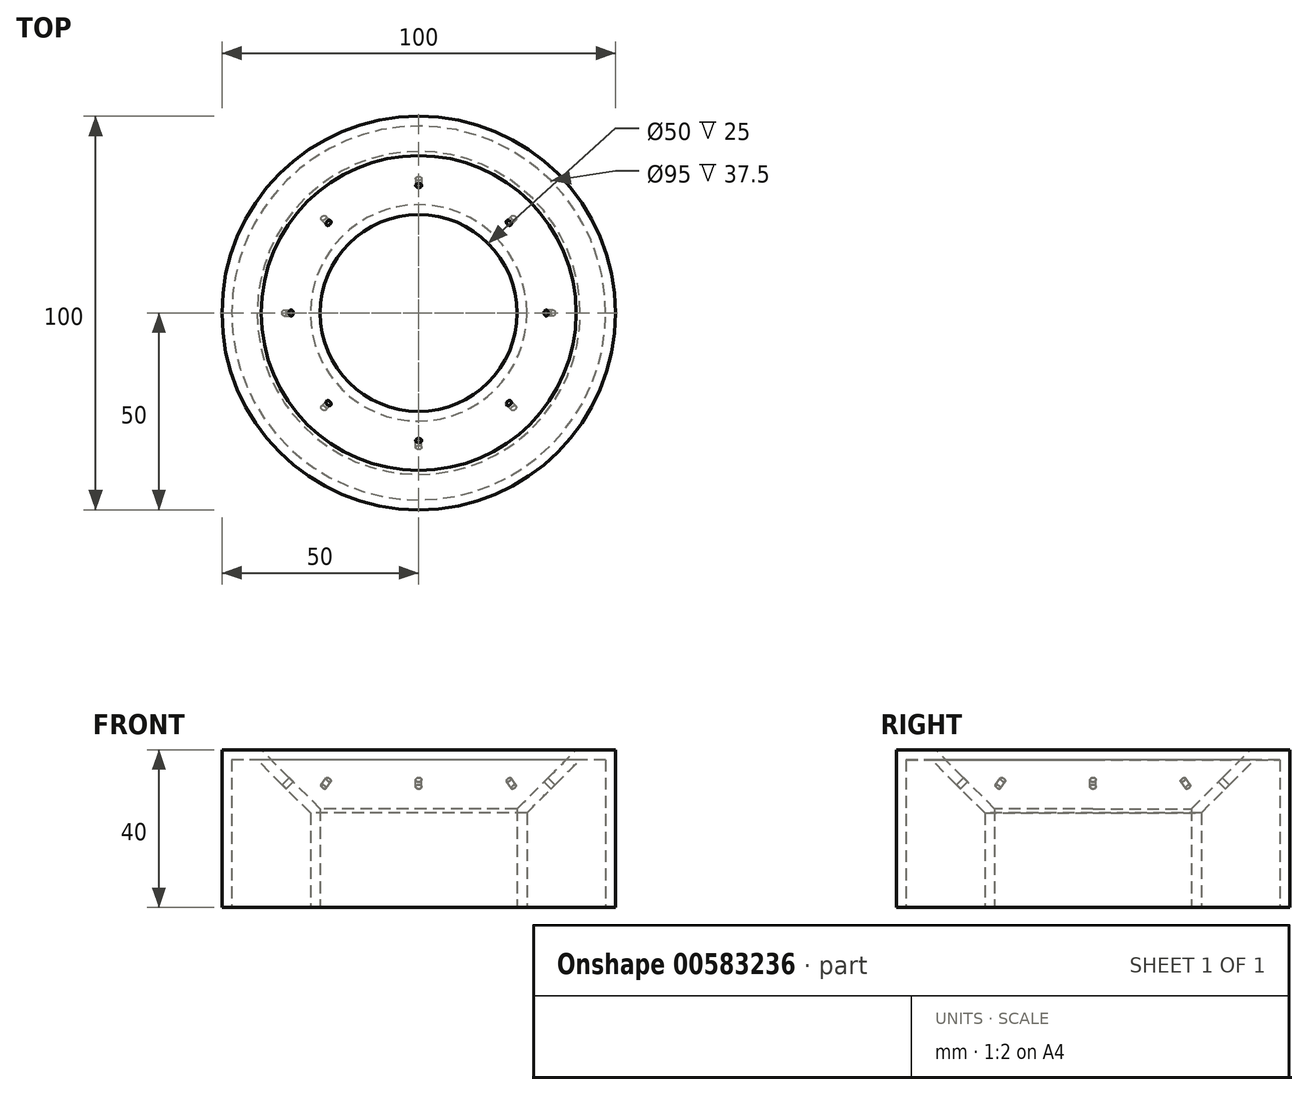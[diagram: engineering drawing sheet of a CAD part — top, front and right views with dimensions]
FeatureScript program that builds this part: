
annotation { "Feature Type Name" : "Feature", "Feature Type Description" : "" }
export const myFeature = defineFeature(function(context is Context, id is Id, definition is map)
    precondition{}
    {
        {
            var Q0;
            Q0=qCreatedBy(makeId("Top.planeOp"),FACE);
            var sketch = newSketch(context, id + "F0", { "sketchPlane" : qUnion([Q0])});
            skCircle(sketch, "E0", {"center": v(0, 0) * mm, "radius": 50 * mm});
            skSolve(sketch);
        }
        {
            var Q0;
            Q0=qSketchRegion(id+"F0",true);
            extrude(context, id + "F1", {"entities" : qUnion([Q0]), "depth" : 40 * mm, "offsetDistance" : 25 * mm});
        }
        {
            var Q0;
            Q0=makeQuery(id+"F1.opExtrude","CAP_FACE",FACE,{"disambiguationData":[OSD([sQuery(id+"F0.wireOp",EDGE,"E0")])],"isStart":true});
            var sketch = newSketch(context, id + "F2", { "sketchPlane" : qUnion([Q0])});
            skCircle(sketch, "E1.0", {"center": v(0, 0) * mm, "radius": 25 * mm});
            skSolve(sketch);
        }
        {
            var Q0;
            Q0=makeQuery(id+"F2.imprint","IMPRINT",FACE,{"disambiguationData":[TD([[makeQuery(id+"F2.imprint","IMPRINT",EDGE,{"derivedFrom":sQuery(id+"F2.wireOp",EDGE,"E1.0")}),1.0]])]});
            extrude(context, id + "F3", {"entities" : qUnion([Q0]), "operationType" : NewBodyOperationType.REMOVE, "oppositeDirection" : true, "depth" : 50 * mm, "offsetDistance" : 25 * mm});
        }
        {
            var Q0;
            Q0=makeQuery(id+"F1.opExtrude","CAP_FACE",FACE,{"disambiguationData":[OSD([sQuery(id+"F0.wireOp",EDGE,"E0")])],"isStart":false});
            var sketch = newSketch(context, id + "F4", { "sketchPlane" : qUnion([Q0])});
            skCircle(sketch, "E2.0", {"center": v(0, 0) * mm, "radius": 40 * mm});
            skSolve(sketch);
        }
        {
            var Q0;
            Q0=makeQuery(id+"F3.boolean.opBoolean","INTERSECT",EDGE,{"derivedFrom":[makeQuery(id+"F1.opExtrude","CAP_FACE",FACE,{"disambiguationData":[OSD([sQuery(id+"F0.wireOp",EDGE,"E0")])],"isStart":false}),makeQuery(id+"F3.opExtrude","SWEPT_FACE",FACE,{"disambiguationData":[OSD([sQuery(id+"F2.wireOp",EDGE,"E1.0")])]})]});
            chamfer(context, id + "F5", {"entities" : qUnion([Q0]), "width" : 15 * mm, "tangentPropagation" : true});
        }
        {
            var Q0;
            Q0=makeQuery(id+"F1.opExtrude","CAP_FACE",FACE,{"disambiguationData":[OSD([sQuery(id+"F0.wireOp",EDGE,"E0")])],"isStart":true});
            shell(context, id + "F6", {"entities" : qUnion([Q0]), "thickness" : 2.5 * mm});
        }
        {
            var Q0;
            Q0=makeQuery(id+"F4.imprint","IMPRINT",FACE,{"disambiguationData":[TD([[makeQuery(id+"F4.imprint","IMPRINT",EDGE,{"derivedFrom":sQuery(id+"F4.wireOp",EDGE,"E2.0")}),-1.0]])]});
            cPlane(context, id + "F7", {"entities" : qUnion([Q0]), "cplaneType" : CPlaneType.OFFSET, "offset" : 7.5 * mm, "oppositeDirection" : true, "width" : 150 * mm, "height" : 150 * mm});
        }
        {
            var Q0;
            Q0=qCreatedBy(id+"F7.planeOp",FACE);
            var sketch = newSketch(context, id + "F8", { "sketchPlane" : qUnion([Q0])});
            skCircle(sketch, "E3", {"center": v(0, 0) * mm, "radius": 31.23 * mm});
            skLineSegment(sketch, "E4", {"start": v(-56.05, 31.23) * mm, "end": v(53.01, 31.23) * mm});
            skSolve(sketch);
        }
        {
            var Q0;
            Q0=sQuery(id+"F8.wireOp",EDGE,"E4");
            cPlane(context, id + "F9", {"entities" : qUnion([Q0]), "cplaneType" : CPlaneType.LINE_ANGLE, "offset" : 25 * mm, "angle" : 45 * degree, "oppositeDirection" : true, "width" : 150 * mm, "height" : 150 * mm});
        }
        {
            var Q0;
            Q0=qCreatedBy(id+"F9.planeOp",FACE);
            var sketch = newSketch(context, id + "F10", { "sketchPlane" : qUnion([Q0])});
            skCircle(sketch, "E5", {"center": v(0, 45.81) * mm, "radius": 0.75 * mm});
            skSolve(sketch);
        }
        {
            var Q0;
            Q0=qSketchRegion(id+"F10",true);
            extrude(context, id + "F11", {"entities" : qUnion([Q0]), "operationType" : NewBodyOperationType.REMOVE, "endBound" : BoundingType.SYMMETRIC, "depth" : 30 * mm, "offsetDistance" : 25 * mm});
        }
        {
            var Q0;
            Q0=qCreatedBy(makeId("Front.planeOp"),FACE);
            var sketch = newSketch(context, id + "F12", { "sketchPlane" : qUnion([Q0])});
            skLineSegment(sketch, "E6", {"start": v(0, 0) * mm, "end": v(0, 109.05) * mm, "construction": true});
            skSolve(sketch);
        }
        {
            var Q0;
            Q0=makeQuery(id+"F11.boolean.opBoolean","COPY",FACE,{"derivedFrom":makeQuery(id+"F11.opExtrude","SWEPT_FACE",FACE,{"disambiguationData":[OSD([sQuery(id+"F10.wireOp",EDGE,"E5")])]})});
            var Q1;
            Q1=sQuery(id+"F12.wireOp",EDGE,"E6");
            circularPattern(context, id + "F13", {"patternType" : PatternType.FACE, "faces" : qUnion([Q0]), "axis" : qUnion([Q1]), "angle" : 360 * degree, "instanceCount" : 8, "equalSpace" : true});
        }
    });
